# Revit family: Shower_Base-American_Standard-Townsend-6438AM-FCOL.218
name_source: partatom
category: Plumbing Fixtures
revit_build: Autodesk Revit 2018 (Build: 20170223_1515(x64)
units: mm (PartAtom-declared; Revit-internal decimal feet)

## family parameters
Always vertical = No
Cut with Voids When Loaded = No
OmniClass Number = 23.45.05.14.17
OmniClass Title = Showers
Part Type = Normal
Room Calculation Point = No
Round Connector Dimension = Use Diameter
Shared = Yes
Work Plane-Based = Yes

## types (1)
- 6438AM-FCOL.218
    ADA Compliant = Yes
    Assembly Code = D2010710
    CW Connection = No
    CWFU = 3
    Clearance Between Studding = 1/8"
    Compliance Certifications = Meets or Exceeds the Following Specifications: • CSA B45.5 / IAPMO Z124• IAPMO R&T cUPC• ICC A117.1
    Default Elevation = 0"
    Description = Townsend® 64 x 38-Inch Single Threshold ADA Shower Base With Linear Drain
    Drain Length = 33 1/4"
    Drain Location = 32"
    Drain Material = Non Porous Material-American Standard-218-Soft White
    HW Connection = No
    HWFU = 3
    Installation Type = Floor Mounted
    Length = 38"
    Manufacturer = American Standard
    Material = Non Porous Material-American Standard-218-Soft White
    Model = 6438AM-FCOL.218
    Product Documentation Link = https://americanstandard.box.com
    Product Page URL = https://www.americanstandard.ca
    Shipping Weight = 62.8 Kg. (138 Lbs.)
    Trench Cover Material = Stainless Steel-American Standard-Brushed
    URL = https://www.americanstandard.ca
    Vent Connection = No
    WFU = 4
    Warranty Information = 5-Year Limited Warranty
    Waste Connection = Yes
    Waste Connection Diameter = 3 3/8"
    Width = 64"

## geometry (parser evidence)
native form markers: Sweep x3
no freeform markers — native parametric forms only
